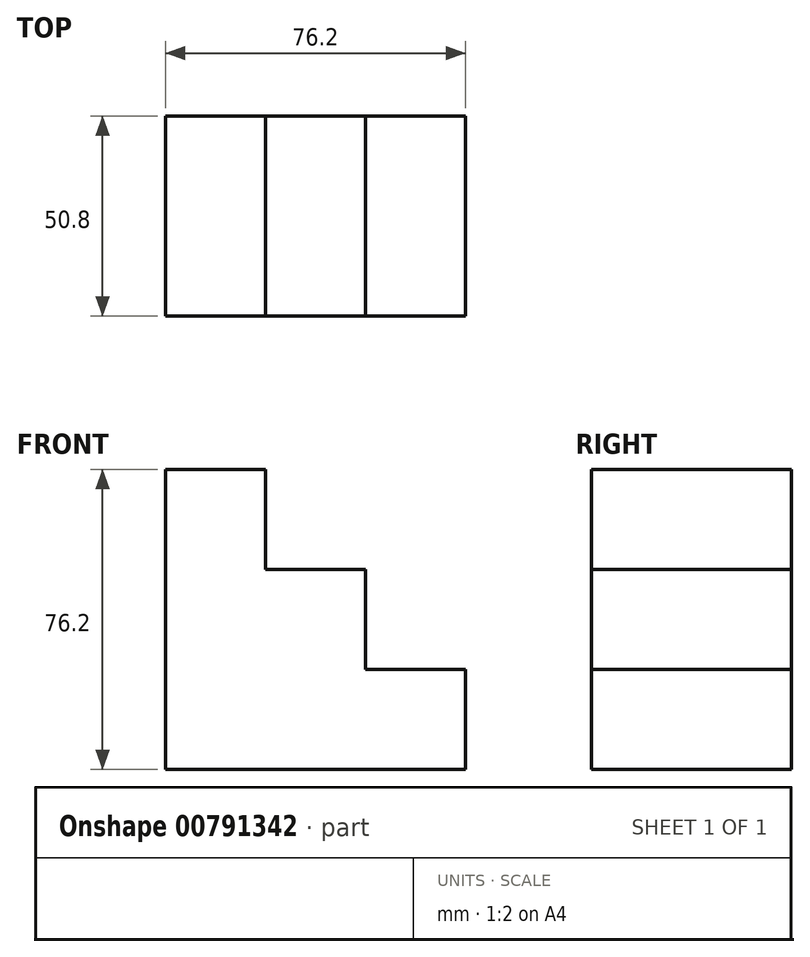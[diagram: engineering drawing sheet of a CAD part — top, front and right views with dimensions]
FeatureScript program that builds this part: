
annotation { "Feature Type Name" : "Feature", "Feature Type Description" : "" }
export const myFeature = defineFeature(function(context is Context, id is Id, definition is map)
    precondition{}
    {
        {
            var Q0;
            Q0=qCreatedBy(makeId("Front.planeOp"),FACE);
            var sketch = newSketch(context, id + "F0", { "sketchPlane" : qUnion([Q0])});
            skLineSegment(sketch, "E0", {"start": v(0, 76.2) * mm, "end": v(0, 0) * mm});
            skLineSegment(sketch, "E1", {"start": v(0, 0) * mm, "end": v(76.2, 0) * mm});
            skLineSegment(sketch, "E2", {"start": v(0, 76.2) * mm, "end": v(25.4, 76.2) * mm});
            skLineSegment(sketch, "E3", {"start": v(25.4, 76.2) * mm, "end": v(25.4, 50.8) * mm});
            skLineSegment(sketch, "E4", {"start": v(25.4, 50.8) * mm, "end": v(50.8, 50.8) * mm});
            skLineSegment(sketch, "E5", {"start": v(50.8, 50.8) * mm, "end": v(50.8, 25.4) * mm});
            skLineSegment(sketch, "E6", {"start": v(50.8, 25.4) * mm, "end": v(76.2, 25.4) * mm});
            skLineSegment(sketch, "E7", {"start": v(76.2, 25.4) * mm, "end": v(76.2, 0) * mm});
            skSolve(sketch);
        }
        {
            var Q0;
            Q0=qSketchRegion(id+"F0",true);
            extrude(context, id + "F1", {"entities" : qUnion([Q0]), "depth" : 50.8 * mm, "offsetDistance" : 25.4 * mm});
        }
    });
